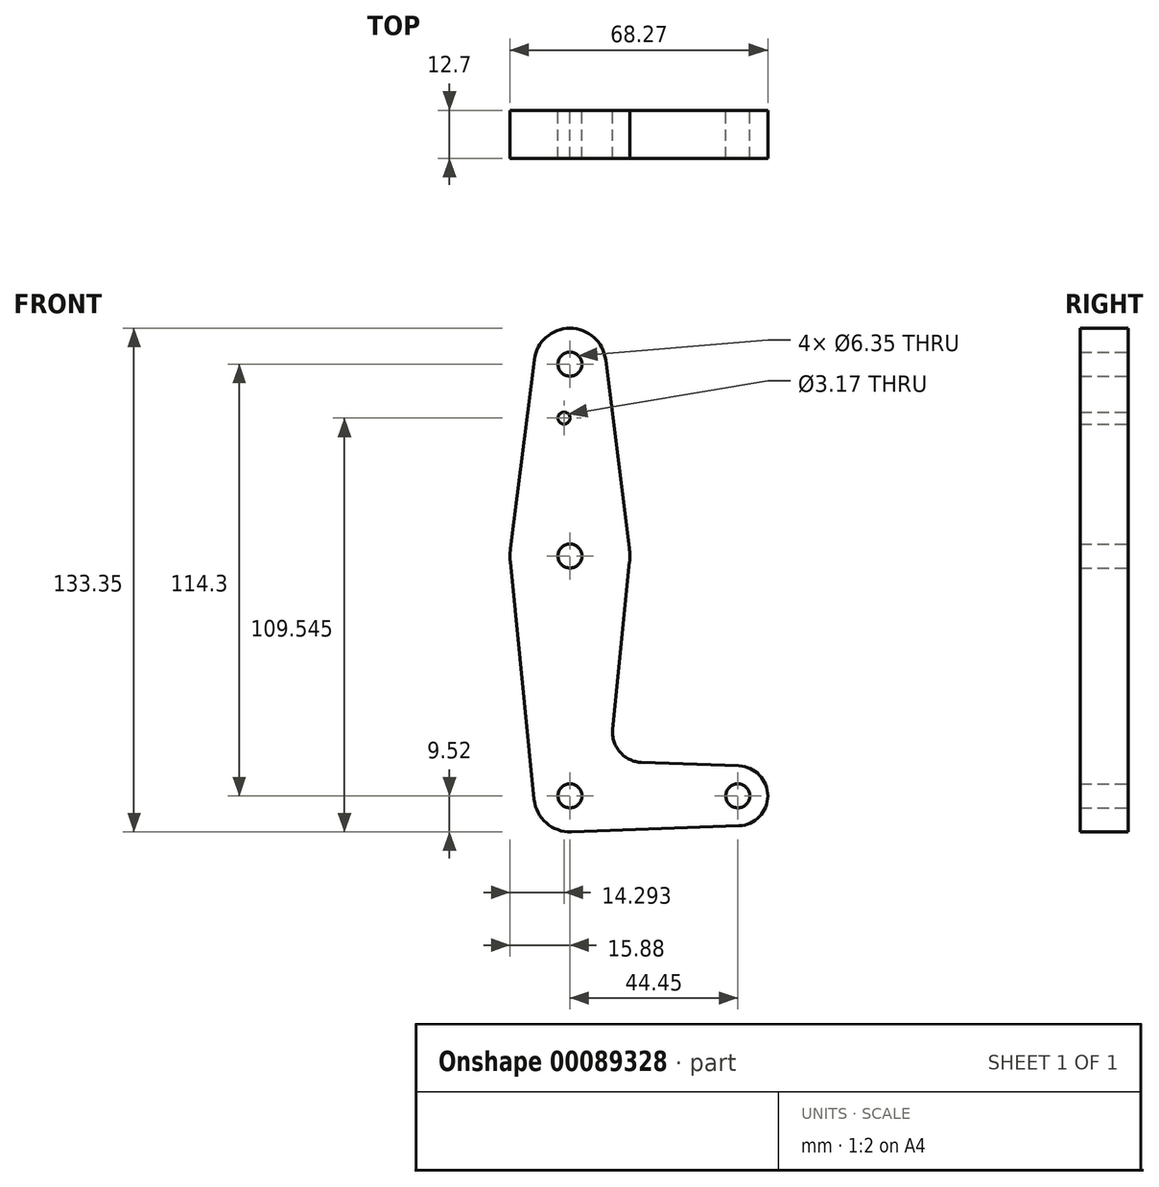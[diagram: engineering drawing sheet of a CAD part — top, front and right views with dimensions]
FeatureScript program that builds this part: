
annotation { "Feature Type Name" : "Feature", "Feature Type Description" : "" }
export const myFeature = defineFeature(function(context is Context, id is Id, definition is map)
    precondition{}
    {
        {
            var Q0;
            Q0=qCreatedBy(makeId("Front.planeOp"),FACE);
            var sketch = newSketch(context, id + "F0", { "sketchPlane" : qUnion([Q0])});
            skCircle(sketch, "E0", {"center": v(0, 63.5) * mm, "radius": 15.88 * mm});
            skCircle(sketch, "E1", {"center": v(0, 114.3) * mm, "radius": 9.53 * mm});
            skCircle(sketch, "E2", {"center": v(0, 0) * mm, "radius": 9.53 * mm});
            skCircle(sketch, "E3", {"center": v(44.45, 0) * mm, "radius": 7.94 * mm});
            skLineSegment(sketch, "E4", {"start": v(-9.45, 115.5) * mm, "end": v(-15.75, 65.48) * mm});
            skLineSegment(sketch, "E5", {"start": v(9.45, 115.5) * mm, "end": v(15.75, 65.48) * mm});
            skLineSegment(sketch, "E6", {"start": v(-15.8, 61.91) * mm, "end": v(-9.48, -0.95) * mm});
            skLineSegment(sketch, "E7", {"start": v(15.8, 61.91) * mm, "end": v(11.34, 17.6) * mm});
            skLineSegment(sketch, "E8", {"start": v(0.34, -9.52) * mm, "end": v(44.73, -7.93) * mm});
            skCircle(sketch, "E9", {"center": v(-1.59, 100.03) * mm, "radius": 1.59 * mm});
            skCircle(sketch, "E10", {"center": v(0, 114.3) * mm, "radius": 3.17 * mm});
            skCircle(sketch, "E11", {"center": v(0, 63.5) * mm, "radius": 3.17 * mm});
            skCircle(sketch, "E12", {"center": v(0, 0) * mm, "radius": 3.17 * mm});
            skCircle(sketch, "E13", {"center": v(-96.86, -59.92) * mm, "radius": 3.17 * mm});
            skCircle(sketch, "E14", {"center": v(44.45, 0) * mm, "radius": 3.17 * mm});
            skArc(sketch, "E15", {"start": v(11.34, 17.6) * mm, "mid": v(13.26, 11.57) * mm, "end": v(18.97, 8.85) * mm});
            skLineSegment(sketch, "E16.trimOffspring", {"start": v(18.97, 8.85) * mm, "end": v(44.73, 7.93) * mm});
            skLineSegment(sketch, "E17", {"start": v(0, 114.3) * mm, "end": v(0, 63.5) * mm});
            skSolve(sketch);
        }
        {
            var Q0;
            Q0=makeQuery(id+"F0.imprint","IMPRINT",FACE,{"disambiguationData":[TD([[makeQuery(id+"F0.imprint","IMPRINT",EDGE,{"derivedFrom":sQuery(id+"F0.wireOp",EDGE,"E13")}),1.0]])]});
            var Q1;
            Q1=makeQuery(id+"F0.imprint","IMPRINT",FACE,{"disambiguationData":[TD([[makeQuery(id+"F0.imprint","IMPRINT",EDGE,{"derivedFrom":sQuery(id+"F0.wireOp",EDGE,"E12")}),-1.0]])]});
            var Q2;
            Q2=makeQuery(id+"F0.imprint","IMPRINT",FACE,{"disambiguationData":[TD([[makeQuery(id+"F0.imprint","IMPRINT",EDGE,{"derivedFrom":sQuery(id+"F0.wireOp",EDGE,"E14")}),-1.0]])]});
            var Q3;
            {var subQ0=sQuery(id+"F0.wireOp",EDGE,"E6");Q3=makeQuery(id+"F0.imprint","IMPRINT",FACE,{"disambiguationData":[TD([[makeQuery(id+"F0.imprint","IMPRINT",EDGE,{"derivedFrom":subQ0}),1.0]])]});}
            var Q4;
            {var subQ4=sQuery(id+"F0.wireOp",EDGE,"E5");Q4=makeQuery(id+"F0.imprint","IMPRINT",FACE,{"disambiguationData":[TD([[makeQuery(id+"F0.imprint","IMPRINT",EDGE,{"derivedFrom":subQ4}),-1.0]])]});}
            var Q5;
            Q5=makeQuery(id+"F0.imprint","IMPRINT",FACE,{"disambiguationData":[TD([[makeQuery(id+"F0.imprint","IMPRINT",EDGE,{"derivedFrom":sQuery(id+"F0.wireOp",EDGE,"E10")}),-1.0]])]});
            var Q6;
            Q6=makeQuery(id+"F0.imprint","IMPRINT",FACE,{"disambiguationData":[TD([[makeQuery(id+"F0.imprint","IMPRINT",EDGE,{"derivedFrom":sQuery(id+"F0.wireOp",EDGE,"E11")}),-1.0]])]});
            var Q7;
            {var subQ0=sQuery(id+"F0.wireOp",EDGE,"E4");Q7=makeQuery(id+"F0.imprint","IMPRINT",FACE,{"disambiguationData":[TD([[makeQuery(id+"F0.imprint","IMPRINT",EDGE,{"derivedFrom":subQ0}),1.0]])]});}
            extrude(context, id + "F1", {"entities" : qUnion([Q0, Q1, Q2, Q3, Q4, Q5, Q6, Q7]), "depth" : 12.7 * mm});
        }
        {
            var Q0;
            Q0=makeQuery(id+"F1.opExtrude","SWEPT_BODY",BODY,{"disambiguationData":[OSD([sQuery(id+"F0.wireOp",EDGE,"E13")])]});
            deleteBodies(context, id + "F2", {"entities" : qUnion([Q0])});
        }
    });
